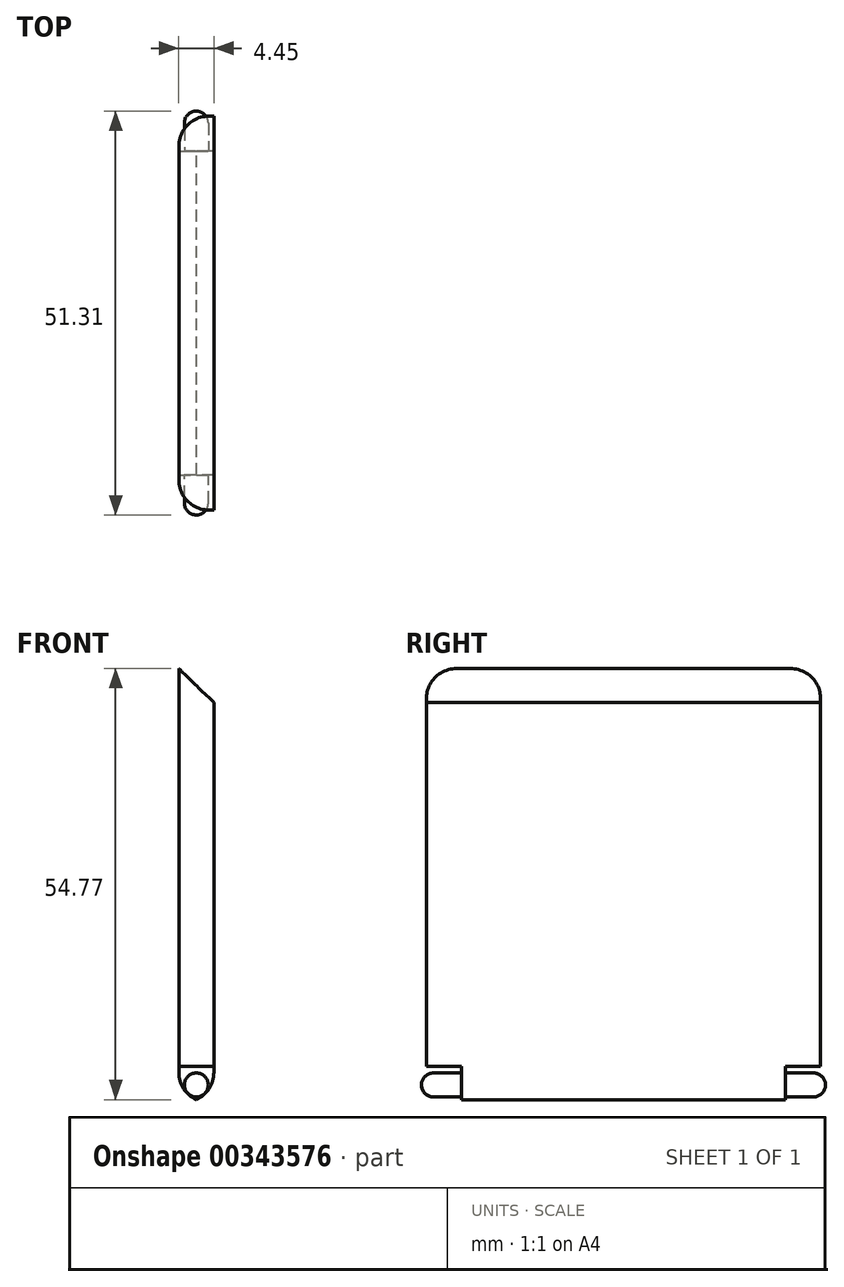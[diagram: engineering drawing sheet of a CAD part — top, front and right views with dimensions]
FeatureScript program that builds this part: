
annotation { "Feature Type Name" : "Feature", "Feature Type Description" : "" }
export const myFeature = defineFeature(function(context is Context, id is Id, definition is map)
    precondition{}
    {
        {
            var Q0;
            Q0=qCreatedBy(makeId("Front.planeOp"),FACE);
            var sketch = newSketch(context, id + "F0", { "sketchPlane" : qUnion([Q0])});
            skLineSegment(sketch, "E0.bottom", {"start": v(0, 0) * mm, "end": v(-4.45, 0) * mm});
            skLineSegment(sketch, "E0.top", {"start": v(0, 50.8) * mm, "end": v(-4.45, 50.8) * mm});
            skLineSegment(sketch, "E0.left", {"start": v(0, 0) * mm, "end": v(0, 50.8) * mm});
            skLineSegment(sketch, "E0.right", {"start": v(-4.45, 0) * mm, "end": v(-4.45, 50.8) * mm});
            skSolve(sketch);
        }
        {
            var Q0;
            Q0 = qSketchRegion(id + "F0", true);
            extrude(context, id + "F1", {"entities" : qUnion([Q0]), "depth" : 41.15 * mm, "offsetDistance" : 25.4 * mm});
        }
        {
            var Q0;
            Q0=makeQuery(id+"F1.opExtrude","SWEPT_FACE",FACE,{"disambiguationData":[OSD([sQuery(id+"F0.wireOp",EDGE,"E0.right")])]});
            var sketch = newSketch(context, id + "F2", { "sketchPlane" : qUnion([Q0])});
            skLineSegment(sketch, "E1", {"start": v(41.15, 0) * mm, "end": v(41.15, 4.57) * mm});
            skLineSegment(sketch, "E2", {"start": v(41.15, 4.57) * mm, "end": v(45.6, 4.57) * mm});
            skLineSegment(sketch, "E3.bottom", {"start": v(45.6, 4.57) * mm, "end": v(41.15, 4.57) * mm});
            skLineSegment(sketch, "E3.top", {"start": v(45.6, 50.8) * mm, "end": v(41.15, 50.8) * mm});
            skLineSegment(sketch, "E3.left", {"start": v(45.6, 4.57) * mm, "end": v(45.6, 50.8) * mm});
            skLineSegment(sketch, "E3.right", {"start": v(41.15, 4.57) * mm, "end": v(41.15, 50.8) * mm});
            skSolve(sketch);
        }
        {
            var Q0;
            Q0 = qSketchRegion(id + "F2", true);
            extrude(context, id + "F3", {"entities" : qUnion([Q0]), "operationType" : NewBodyOperationType.ADD, "depth" : -4.44 * mm, "offsetDistance" : 25.4 * mm});
        }
        {
            var Q0;
            Q0=makeQuery(id+"F3.boolean.opBoolean","MERGE",FACE,{"derivedFrom":[makeQuery(id+"F1.opExtrude","SWEPT_FACE",FACE,{"disambiguationData":[OSD([sQuery(id+"F0.wireOp",EDGE,"E0.right")])]}),makeQuery(id+"F3.opExtrude","CAP_FACE",FACE,{"disambiguationData":[OSD([sQuery(id+"F2.wireOp",EDGE,"E3.bottom"),sQuery(id+"F2.wireOp",EDGE,"E3.top"),sQuery(id+"F2.wireOp",EDGE,"E3.left"),sQuery(id+"F2.wireOp",EDGE,"E3.right")])],"isStart":true})]});
            var sketch = newSketch(context, id + "F4", { "sketchPlane" : qUnion([Q0])});
            skLineSegment(sketch, "E4", {"start": v(0, 0) * mm, "end": v(0, 4.57) * mm});
            skLineSegment(sketch, "E5", {"start": v(0, 4.57) * mm, "end": v(-4.45, 4.57) * mm});
            skLineSegment(sketch, "E6.bottom", {"start": v(-4.45, 4.57) * mm, "end": v(0, 4.57) * mm});
            skLineSegment(sketch, "E6.top", {"start": v(-4.44, 50.8) * mm, "end": v(0, 50.8) * mm});
            skLineSegment(sketch, "E6.left", {"start": v(-4.44, 4.57) * mm, "end": v(-4.44, 50.8) * mm});
            skLineSegment(sketch, "E6.right", {"start": v(0, 4.57) * mm, "end": v(0, 50.8) * mm});
            skSolve(sketch);
        }
        {
            var Q0;
            Q0 = qSketchRegion(id + "F4", true);
            extrude(context, id + "F5", {"entities" : qUnion([Q0]), "operationType" : NewBodyOperationType.ADD, "depth" : -4.44 * mm, "offsetDistance" : 25.4 * mm});
        }
        {
            var Q0;
            Q0=makeQuery(id+"F1.opExtrude","CAP_FACE",FACE,{"disambiguationData":[OSD([sQuery(id+"F0.wireOp",EDGE,"E0.bottom"),sQuery(id+"F0.wireOp",EDGE,"E0.top"),sQuery(id+"F0.wireOp",EDGE,"E0.left"),sQuery(id+"F0.wireOp",EDGE,"E0.right")])],"isStart":true});
            var sketch = newSketch(context, id + "F6", { "sketchPlane" : qUnion([Q0])});
            skLineSegment(sketch, "E7", {"start": v(4.45, 0) * mm, "end": v(0, 0) * mm});
            skLineSegment(sketch, "E8", {"start": v(0, 0) * mm, "end": v(2.22, 0) * mm});
            skLineSegment(sketch, "E9", {"start": v(2.22, 0) * mm, "end": v(2.22, 4.45) * mm});
            skLineSegment(sketch, "E10", {"start": v(2.22, 4.45) * mm, "end": v(2.22, 2.22) * mm});
            skCircle(sketch, "E11", {"center": v(2.22, 2.22) * mm, "radius": 1.52 * mm});
            skSolve(sketch);
        }
        {
            var Q0;
            Q0 = qSketchRegion(id + "F6", true);
            extrude(context, id + "F7", {"entities" : qUnion([Q0]), "operationType" : NewBodyOperationType.ADD, "depth" : 5.08 * mm, "offsetDistance" : 25.4 * mm});
        }
        {
            var Q0;
            Q0=makeQuery(id+"F1.opExtrude","CAP_FACE",FACE,{"disambiguationData":[OSD([sQuery(id+"F0.wireOp",EDGE,"E0.bottom"),sQuery(id+"F0.wireOp",EDGE,"E0.top"),sQuery(id+"F0.wireOp",EDGE,"E0.left"),sQuery(id+"F0.wireOp",EDGE,"E0.right")])],"isStart":false});
            var sketch = newSketch(context, id + "F8", { "sketchPlane" : qUnion([Q0])});
            skLineSegment(sketch, "E12", {"start": v(-4.45, 0) * mm, "end": v(0, 0) * mm});
            skLineSegment(sketch, "E13", {"start": v(0, 0) * mm, "end": v(-2.22, 0) * mm});
            skLineSegment(sketch, "E14", {"start": v(-2.22, 0) * mm, "end": v(-2.22, 4.45) * mm});
            skLineSegment(sketch, "E15", {"start": v(-2.22, 4.45) * mm, "end": v(-2.22, 2.22) * mm});
            skCircle(sketch, "E16", {"center": v(-2.22, 2.22) * mm, "radius": 1.52 * mm});
            skSolve(sketch);
        }
        {
            var Q0;
            Q0 = qSketchRegion(id + "F8", true);
            extrude(context, id + "F9", {"entities" : qUnion([Q0]), "operationType" : NewBodyOperationType.ADD, "depth" : 5.08 * mm, "offsetDistance" : 25.4 * mm});
        }
        {
            var Q0;
            Q0=makeQuery(id+"F7.opExtrude","CAP_EDGE",EDGE,{"disambiguationData":[OSD([sQuery(id+"F6.wireOp",EDGE,"E11")])],"isStart":false});
            var Q1;
            Q1=makeQuery(id+"F9.opExtrude","CAP_EDGE",EDGE,{"disambiguationData":[OSD([sQuery(id+"F8.wireOp",EDGE,"E16")])],"isStart":false});
            fillet(context, id + "F10", {"entities" : qUnion([Q0, Q1]), "radius" : 1.52 * mm, "tangentPropagation" : true, "rho" : 0, "crossSection" : FilletCrossSection.CONIC, "allowEdgeOverflow" : false});
        }
        {
            var Q0;
            Q0=makeQuery(id+"F3.opExtrude","SWEPT_FACE",FACE,{"disambiguationData":[OSD([sQuery(id+"F2.wireOp",EDGE,"E3.left")])]});
            var sketch = newSketch(context, id + "F11", { "sketchPlane" : qUnion([Q0])});
            skLineSegment(sketch, "E17", {"start": v(-4.45, 50.8) * mm, "end": v(-4.45, 55.12) * mm});
            skLineSegment(sketch, "E18", {"start": v(-4.45, 55.12) * mm, "end": v(0, 50.8) * mm});
            skSolve(sketch);
        }
        {
            var Q0;
            Q0 = qSketchRegion(id + "F11", true);
            var Q1;
            Q1=makeQuery(id+"F11.imprint","IMPRINT",FACE,{"disambiguationData":[TD([[makeQuery(id+"F11.imprint","IMPRINT",EDGE,{"derivedFrom":sQuery(id+"F11.wireOp",EDGE,"E17")}),-1.0]])]});
            extrude(context, id + "F12", {"entities" : qUnion([Q0, Q1]), "operationType" : NewBodyOperationType.ADD, "depth" : -50.04 * mm, "offsetDistance" : 25.4 * mm});
        }
        {
            var Q0;
            Q0=makeQuery(id+"F1.opExtrude","SWEPT_EDGE",EDGE,{"disambiguationData":[OSD([sQuery(id+"F0.wireOp",EDGE,"E0.bottom"),sQuery(id+"F0.wireOp",EDGE,"E0.right")])]});
            var Q1;
            Q1=makeQuery(id+"F1.opExtrude","SWEPT_EDGE",EDGE,{"disambiguationData":[OSD([sQuery(id+"F0.wireOp",EDGE,"E0.bottom"),sQuery(id+"F0.wireOp",EDGE,"E0.left")])]});
            var Q2;
            Q2=makeQuery(id+"F12.boolean.opBoolean","MERGE",EDGE,{"derivedFrom":[makeQuery(id+"F5.opExtrude","CAP_EDGE",EDGE,{"disambiguationData":[OSD([sQuery(id+"F4.wireOp",EDGE,"E6.left")])],"isStart":true}),makeQuery(id+"F12.opExtrude","CAP_EDGE",EDGE,{"disambiguationData":[OSD([sQuery(id+"F11.wireOp",EDGE,"E17")])],"isStart":false})]});
            var Q3;
            Q3=makeQuery(id+"F12.boolean.opBoolean","MERGE",EDGE,{"derivedFrom":[makeQuery(id+"F3.opExtrude","CAP_EDGE",EDGE,{"disambiguationData":[OSD([sQuery(id+"F2.wireOp",EDGE,"E3.left")])],"isStart":true}),makeQuery(id+"F12.opExtrude","CAP_EDGE",EDGE,{"disambiguationData":[OSD([sQuery(id+"F11.wireOp",EDGE,"E17")])],"isStart":true})]});
            fillet(context, id + "F13", {"entities" : qUnion([Q0, Q1, Q2, Q3]), "radius" : 3.8 * mm, "tangentPropagation" : true, "allowEdgeOverflow" : false});
        }
    });
